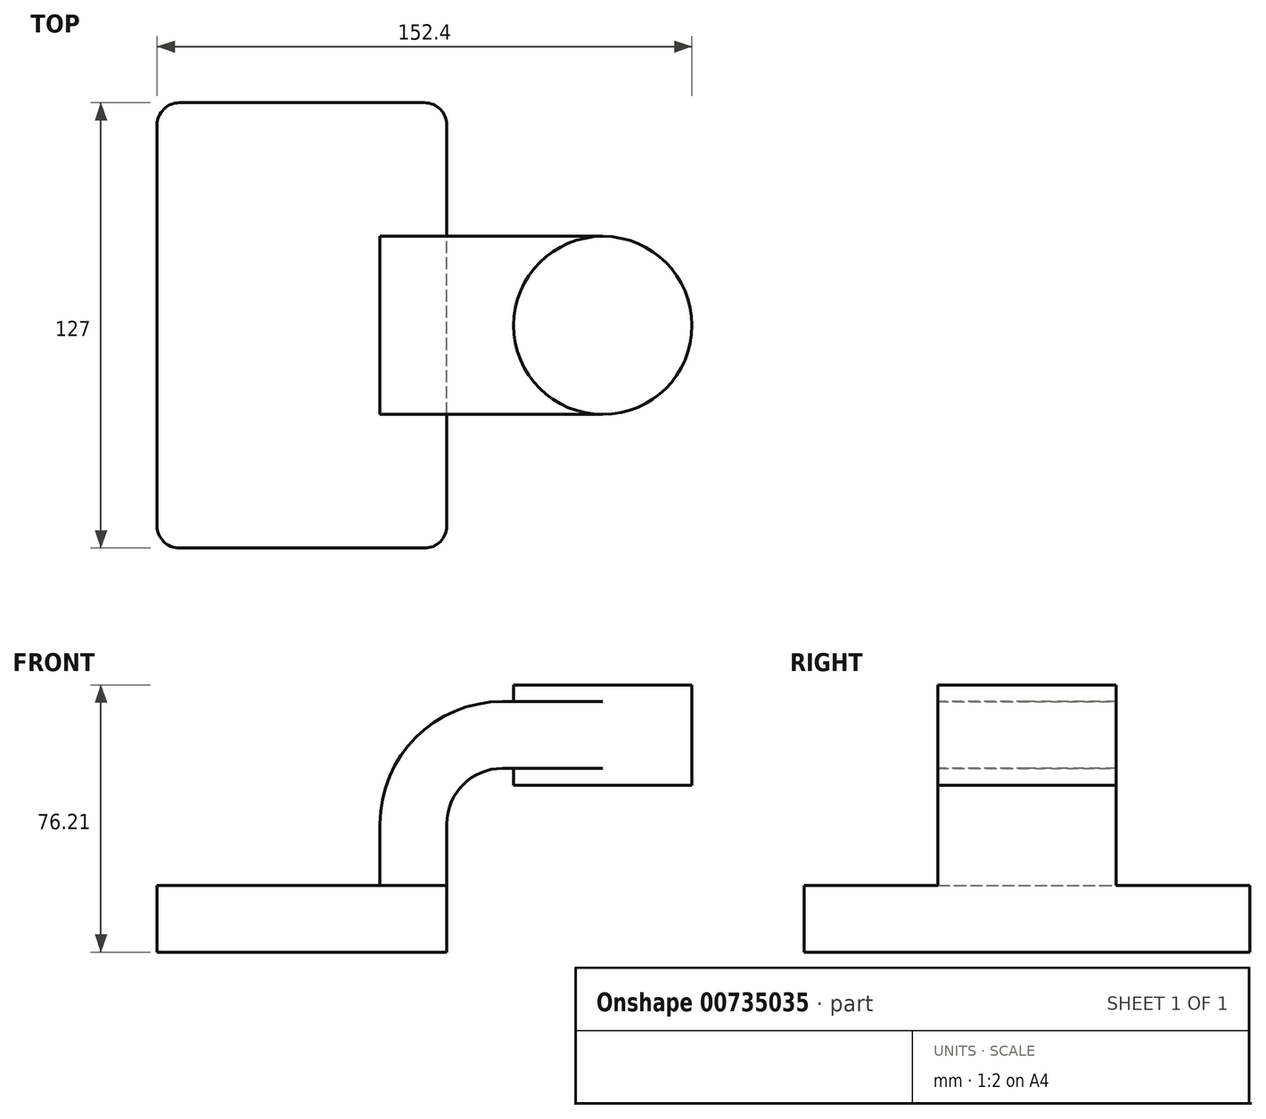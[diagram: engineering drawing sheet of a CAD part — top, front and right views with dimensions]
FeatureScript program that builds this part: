
annotation { "Feature Type Name" : "Feature", "Feature Type Description" : "" }
export const myFeature = defineFeature(function(context is Context, id is Id, definition is map)
    precondition{}
    {
        {
            var Q0;
            Q0=qCreatedBy(makeId("Front.planeOp"),FACE);
            var sketch = newSketch(context, id + "F0", { "sketchPlane" : qUnion([Q0])});
            skLineSegment(sketch, "E0.bottom", {"start": v(41.28, -9.52) * mm, "end": v(-41.28, -9.52) * mm});
            skLineSegment(sketch, "E0.top", {"start": v(41.28, 9.53) * mm, "end": v(-41.28, 9.53) * mm});
            skLineSegment(sketch, "E0.left", {"start": v(41.28, -9.52) * mm, "end": v(41.28, 9.53) * mm});
            skLineSegment(sketch, "E0.right", {"start": v(-41.28, -9.52) * mm, "end": v(-41.28, 9.53) * mm});
            skPoint(sketch, "E0.middle", {"position": v(0, 0) * mm});
            skLineSegment(sketch, "E1.bottom", {"start": v(111.13, 38.1) * mm, "end": v(60.33, 38.1) * mm});
            skLineSegment(sketch, "E1.top", {"start": v(111.13, 66.68) * mm, "end": v(60.33, 66.68) * mm});
            skLineSegment(sketch, "E1.left", {"start": v(111.13, 38.1) * mm, "end": v(111.13, 66.68) * mm});
            skLineSegment(sketch, "E1.right", {"start": v(60.33, 38.1) * mm, "end": v(60.33, 66.68) * mm});
            skPoint(sketch, "E1.middle", {"position": v(85.73, 52.39) * mm});
            skLineSegment(sketch, "E2", {"start": v(41.28, 9.53) * mm, "end": v(41.28, 27) * mm});
            skArc(sketch, "E3", {"start": v(41.27, 27) * mm, "mid": v(45.92, 38.23) * mm, "end": v(57.15, 42.88) * mm});
            skLineSegment(sketch, "E4", {"start": v(57.15, 42.88) * mm, "end": v(85.73, 42.88) * mm});
            skLineSegment(sketch, "E5.0", {"start": v(57.15, 61.93) * mm, "end": v(85.73, 61.93) * mm});
            skArc(sketch, "E5.1", {"start": v(22.22, 27) * mm, "mid": v(32.45, 51.7) * mm, "end": v(57.15, 61.93) * mm});
            skLineSegment(sketch, "E5.2", {"start": v(22.22, 9.53) * mm, "end": v(22.22, 27) * mm});
            skLineSegment(sketch, "E6", {"start": v(85.73, 38.1) * mm, "end": v(85.73, 66.68) * mm});
            skFitSpline(sketch, "E7", {"points": [v(-41.28, 9.52) * mm, v(57.15, 61.93) * mm], "startDerivative": vector(-0.3, 55.96) * mm, "endDerivative": vector(220.62, -1.06) * mm});
            skSolve(sketch);
        }
        {
            var Q0;
            Q0=makeQuery(id+"F0.imprint","IMPRINT",FACE,{"disambiguationData":[TD([[makeQuery(id+"F0.imprint","IMPRINT",EDGE,{"derivedFrom":sQuery(id+"F0.wireOp",EDGE,"E0.bottom")}),-1.0]])]});
            extrude(context, id + "F1", {"entities" : qUnion([Q0]), "endBound" : BoundingType.SYMMETRIC, "depth" : 127 * mm, "offsetDistance" : 25.4 * mm});
        }
        {
            var Q0;
            {var subQ0=sQuery(id+"F0.wireOp",EDGE,"E4");var subQ1=sQuery(id+"F0.wireOp",EDGE,"E1.right");var subQ2=makeQuery(id+"F0.imprint","INTERSECT",VERTEX,{"derivedFrom":[subQ1,subQ0]});Q0=makeQuery(id+"F0.imprint","IMPRINT",FACE,{"disambiguationData":[TD([[makeQuery(id+"F0.imprint","IMPRINT",EDGE,{"disambiguationData":[TD([[subQ2,-1.0]])],"derivedFrom":subQ1}),-1.0]])]});}
            var Q1;
            {var subQ1=sQuery(id+"F0.wireOp",EDGE,"E2");Q1=makeQuery(id+"F0.imprint","IMPRINT",FACE,{"disambiguationData":[TD([[makeQuery(id+"F0.imprint","IMPRINT",EDGE,{"derivedFrom":subQ1}),1.0]])]});}
            extrude(context, id + "F2", {"entities" : qUnion([Q0, Q1]), "operationType" : NewBodyOperationType.ADD, "endBound" : BoundingType.SYMMETRIC, "depth" : 50.8 * mm, "offsetDistance" : 25.4 * mm});
        }
        {
            var Q0;
            Q0=makeQuery(id+"F0.imprint","IMPRINT",FACE,{"disambiguationData":[TD([[makeQuery(id+"F0.imprint","IMPRINT",EDGE,{"derivedFrom":sQuery(id+"F0.wireOp",EDGE,"E5.1")}),1.0]])]});
            extrude(context, id + "F3", {"entities" : qUnion([Q0]), "operationType" : NewBodyOperationType.ADD, "endBound" : BoundingType.SYMMETRIC, "depth" : 15.88 * mm, "offsetDistance" : 25.4 * mm});
        }
        {
            var Q0;
            {var subQ4=sQuery(id+"F0.wireOp",EDGE,"E1.left");Q0=makeQuery(id+"F0.imprint","IMPRINT",FACE,{"disambiguationData":[TD([[makeQuery(id+"F0.imprint","IMPRINT",EDGE,{"derivedFrom":subQ4}),1.0]])]});}
            var Q1;
            Q1=sQuery(id+"F0.wireOp",EDGE,"E6");
            revolve(context, id + "F4", {"operationType" : NewBodyOperationType.ADD, "surfaceOperationType" : NewSurfaceOperationType.NEW, "entities" : qUnion([Q0]), "axis" : qUnion([Q1]), "revolveType" : RevolveType.FULL});
        }
        {
            var Q0;
            Q0=makeQuery(id+"F1.opExtrude","CAP_EDGE",EDGE,{"disambiguationData":[OSD([sQuery(id+"F0.wireOp",EDGE,"E0.left")])],"isStart":true});
            var Q1;
            Q1=makeQuery(id+"F1.opExtrude","CAP_EDGE",EDGE,{"disambiguationData":[OSD([sQuery(id+"F0.wireOp",EDGE,"E0.right")])],"isStart":true});
            var Q2;
            Q2=makeQuery(id+"F1.opExtrude","CAP_EDGE",EDGE,{"disambiguationData":[OSD([sQuery(id+"F0.wireOp",EDGE,"E0.left")])],"isStart":false});
            var Q3;
            Q3=makeQuery(id+"F1.opExtrude","CAP_EDGE",EDGE,{"disambiguationData":[OSD([sQuery(id+"F0.wireOp",EDGE,"E0.right")])],"isStart":false});
            fillet(context, id + "F5", {"entities" : qUnion([Q0, Q1, Q2, Q3]), "radius" : 6.35 * mm, "tangentPropagation" : true, "allowEdgeOverflow" : false});
        }
    });
